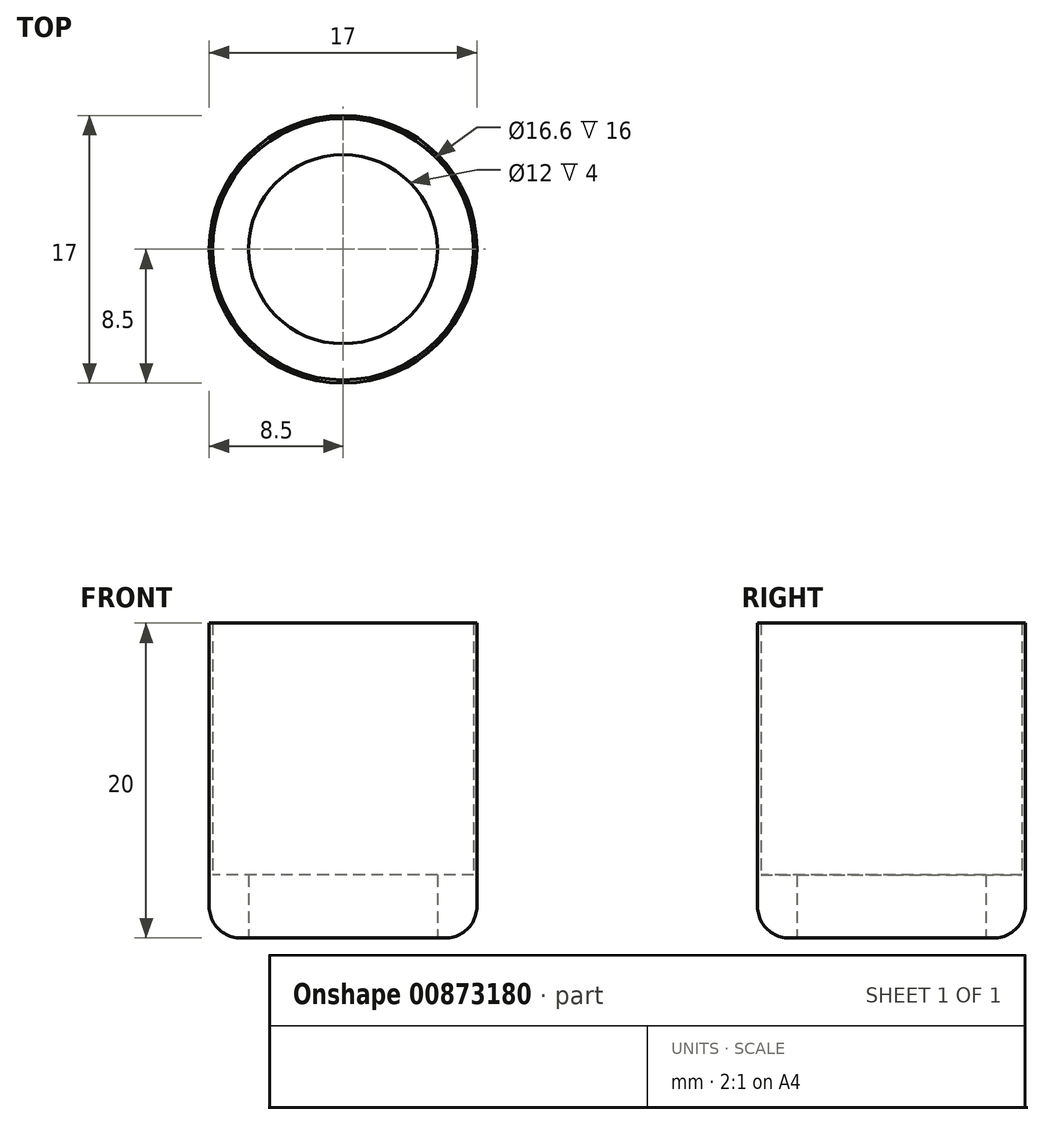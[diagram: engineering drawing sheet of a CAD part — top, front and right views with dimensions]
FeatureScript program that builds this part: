
annotation { "Feature Type Name" : "Feature", "Feature Type Description" : "" }
export const myFeature = defineFeature(function(context is Context, id is Id, definition is map)
    precondition{}
    {
        {
            var Q0;
            Q0=qCreatedBy(makeId("Top.planeOp"),FACE);
            var sketch = newSketch(context, id + "F0", { "sketchPlane" : qUnion([Q0])});
            skCircle(sketch, "E0", {"center": v(0, 0) * mm, "radius": 8.3 * mm});
            skCircle(sketch, "E1", {"center": v(0, 0) * mm, "radius": 8.5 * mm});
            skCircle(sketch, "E2", {"center": v(0, 0) * mm, "radius": 6 * mm});
            skSolve(sketch);
        }
        {
            var Q0;
            Q0=makeQuery(id+"F0.imprint","IMPRINT",FACE,{"disambiguationData":[TD([[makeQuery(id+"F0.imprint","IMPRINT",EDGE,{"derivedFrom":sQuery(id+"F0.wireOp",EDGE,"E0")}),-1.0]])]});
            extrude(context, id + "F1", {"entities" : qUnion([Q0]), "depth" : 20 * mm, "offsetDistance" : 25 * mm});
        }
        {
            var Q0;
            Q0=makeQuery(id+"F0.imprint","IMPRINT",FACE,{"disambiguationData":[TD([[makeQuery(id+"F0.imprint","IMPRINT",EDGE,{"derivedFrom":sQuery(id+"F0.wireOp",EDGE,"E0")}),1.0]])]});
            extrude(context, id + "F2", {"entities" : qUnion([Q0]), "operationType" : NewBodyOperationType.ADD, "depth" : 4 * mm, "offsetDistance" : 25 * mm});
        }
        {
            var Q0;
            Q0=makeQuery(id+"F1.opExtrude","CAP_EDGE",EDGE,{"disambiguationData":[OSD([sQuery(id+"F0.wireOp",EDGE,"E1")])],"isStart":true});
            fillet(context, id + "F3", {"entities" : qUnion([Q0]), "radius" : 2 * mm, "tangentPropagation" : true, "allowEdgeOverflow" : false});
        }
    });
